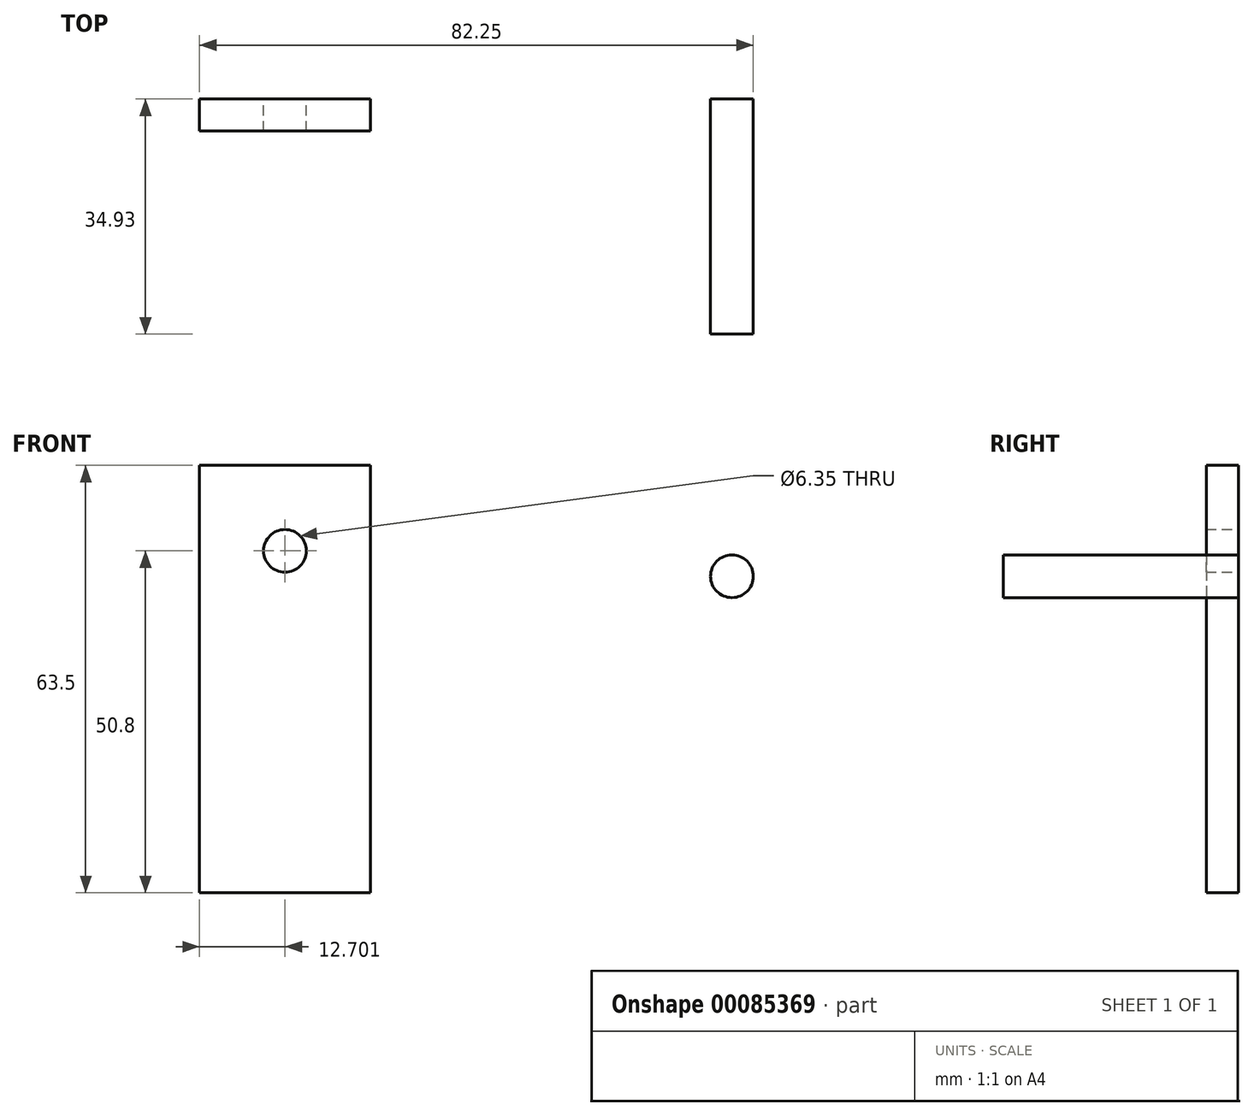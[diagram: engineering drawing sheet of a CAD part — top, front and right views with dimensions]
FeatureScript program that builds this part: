
annotation { "Feature Type Name" : "Feature", "Feature Type Description" : "" }
export const myFeature = defineFeature(function(context is Context, id is Id, definition is map)
    precondition{}
    {
        {
            var Q0;
            Q0=qCreatedBy(makeId("Front.planeOp"),FACE);
            var sketch = newSketch(context, id + "F0", { "sketchPlane" : qUnion([Q0])});
            skLineSegment(sketch, "E0.bottom", {"start": v(-55.14, 39.56) * mm, "end": v(-29.74, 39.56) * mm});
            skLineSegment(sketch, "E0.top", {"start": v(-55.14, -23.94) * mm, "end": v(-29.74, -23.94) * mm});
            skLineSegment(sketch, "E0.left", {"start": v(-55.14, 39.56) * mm, "end": v(-55.14, -23.94) * mm});
            skLineSegment(sketch, "E0.right", {"start": v(-29.74, 39.56) * mm, "end": v(-29.74, -23.94) * mm});
            skCircle(sketch, "E1", {"center": v(-42.44, 26.86) * mm, "radius": 3.18 * mm});
            skSolve(sketch);
        }
        {
            var Q0;
            Q0=makeQuery(id+"F0.imprint","IMPRINT",FACE,{"disambiguationData":[TD([[makeQuery(id+"F0.imprint","IMPRINT",EDGE,{"derivedFrom":sQuery(id+"F0.wireOp",EDGE,"E0.bottom")}),-1.0]])]});
            extrude(context, id + "F1", {"entities" : qUnion([Q0]), "depth" : 4.76 * mm});
        }
        {
            var Q0;
            Q0=qCreatedBy(makeId("Front.planeOp"),FACE);
            var sketch = newSketch(context, id + "F2", { "sketchPlane" : qUnion([Q0])});
            skCircle(sketch, "E2", {"center": v(23.94, 23.09) * mm, "radius": 3.18 * mm});
            skSolve(sketch);
        }
        {
            var Q0;
            Q0=makeQuery(id+"F2.imprint","IMPRINT",FACE,{"disambiguationData":[TD([[makeQuery(id+"F2.imprint","IMPRINT",EDGE,{"derivedFrom":sQuery(id+"F2.wireOp",EDGE,"E2")}),1.0]])]});
            extrude(context, id + "F3", {"entities" : qUnion([Q0]), "depth" : 34.92 * mm});
        }
    });
